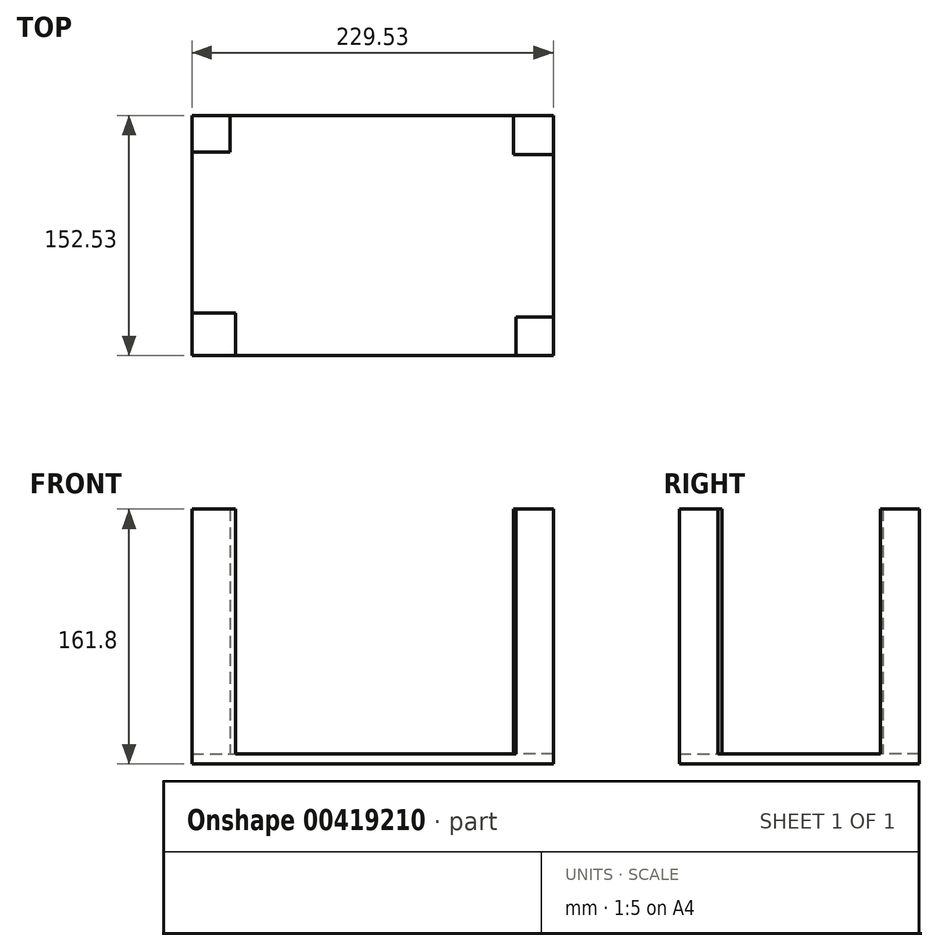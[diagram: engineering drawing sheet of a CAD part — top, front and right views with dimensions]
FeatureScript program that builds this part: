
annotation { "Feature Type Name" : "Feature", "Feature Type Description" : "" }
export const myFeature = defineFeature(function(context is Context, id is Id, definition is map)
    precondition{}
    {
        {
            var Q0;
            Q0=qCreatedBy(makeId("Top.planeOp"),FACE);
            var sketch = newSketch(context, id + "F0", { "sketchPlane" : qUnion([Q0])});
            skLineSegment(sketch, "E0.bottom", {"start": v(-106.06, -80.8) * mm, "end": v(123.47, -80.8) * mm});
            skLineSegment(sketch, "E0.top", {"start": v(-106.06, 71.73) * mm, "end": v(123.47, 71.73) * mm});
            skLineSegment(sketch, "E0.left", {"start": v(-106.06, -80.8) * mm, "end": v(-106.06, 71.73) * mm});
            skLineSegment(sketch, "E0.right", {"start": v(123.47, -80.8) * mm, "end": v(123.47, 71.73) * mm});
            skSolve(sketch);
        }
        {
            var Q0;
            Q0=makeQuery(id+"F0.imprint","IMPRINT",FACE,{"disambiguationData":[TD([[makeQuery(id+"F0.imprint","IMPRINT",EDGE,{"derivedFrom":sQuery(id+"F0.wireOp",EDGE,"E0.bottom")}),1.0]])]});
            extrude(context, id + "F1", {"entities" : qUnion([Q0]), "depth" : 6.35 * mm});
        }
        {
            var Q0;
            Q0=makeQuery(id+"F1.opExtrude","CAP_FACE",FACE,{"disambiguationData":[OSD([sQuery(id+"F0.wireOp",EDGE,"E0.bottom"),sQuery(id+"F0.wireOp",EDGE,"E0.top"),sQuery(id+"F0.wireOp",EDGE,"E0.left"),sQuery(id+"F0.wireOp",EDGE,"E0.right")])],"isStart":false});
            var sketch = newSketch(context, id + "F2", { "sketchPlane" : qUnion([Q0])});
            skLineSegment(sketch, "E1.bottom", {"start": v(123.47, -80.8) * mm, "end": v(99.75, -80.8) * mm});
            skLineSegment(sketch, "E1.top", {"start": v(123.47, -56.12) * mm, "end": v(99.75, -56.12) * mm});
            skLineSegment(sketch, "E1.left", {"start": v(123.47, -80.8) * mm, "end": v(123.47, -56.12) * mm});
            skLineSegment(sketch, "E1.right", {"start": v(99.75, -80.8) * mm, "end": v(99.75, -56.12) * mm});
            skSolve(sketch);
        }
        {
            var Q0;
            Q0=makeQuery(id+"F2.imprint","IMPRINT",FACE,{"disambiguationData":[TD([[makeQuery(id+"F2.imprint","IMPRINT",EDGE,{"derivedFrom":sQuery(id+"F2.wireOp",EDGE,"E1.bottom")}),1.0]])]});
            extrude(context, id + "F3", {"entities" : qUnion([Q0]), "operationType" : NewBodyOperationType.ADD, "depth" : 155.45 * mm});
        }
        {
            var Q0;
            Q0=makeQuery(id+"F1.opExtrude","CAP_FACE",FACE,{"disambiguationData":[OSD([sQuery(id+"F0.wireOp",EDGE,"E0.bottom"),sQuery(id+"F0.wireOp",EDGE,"E0.top"),sQuery(id+"F0.wireOp",EDGE,"E0.left"),sQuery(id+"F0.wireOp",EDGE,"E0.right")])],"isStart":false});
            var sketch = newSketch(context, id + "F4", { "sketchPlane" : qUnion([Q0])});
            skLineSegment(sketch, "E2.bottom", {"start": v(123.47, 71.73) * mm, "end": v(98.13, 71.73) * mm});
            skLineSegment(sketch, "E2.top", {"start": v(123.47, 46.92) * mm, "end": v(98.13, 46.92) * mm});
            skLineSegment(sketch, "E2.left", {"start": v(123.47, 71.73) * mm, "end": v(123.47, 46.92) * mm});
            skLineSegment(sketch, "E2.right", {"start": v(98.13, 71.73) * mm, "end": v(98.13, 46.92) * mm});
            skSolve(sketch);
        }
        {
            var Q0;
            Q0=makeQuery(id+"F4.imprint","IMPRINT",FACE,{"disambiguationData":[TD([[makeQuery(id+"F4.imprint","IMPRINT",EDGE,{"derivedFrom":sQuery(id+"F4.wireOp",EDGE,"E2.bottom")}),-1.0]])]});
            extrude(context, id + "F5", {"entities" : qUnion([Q0]), "operationType" : NewBodyOperationType.ADD, "depth" : 155.45 * mm});
        }
        {
            var Q0;
            Q0=makeQuery(id+"F1.opExtrude","CAP_FACE",FACE,{"disambiguationData":[OSD([sQuery(id+"F0.wireOp",EDGE,"E0.bottom"),sQuery(id+"F0.wireOp",EDGE,"E0.top"),sQuery(id+"F0.wireOp",EDGE,"E0.left"),sQuery(id+"F0.wireOp",EDGE,"E0.right")])],"isStart":false});
            var sketch = newSketch(context, id + "F6", { "sketchPlane" : qUnion([Q0])});
            skLineSegment(sketch, "E3.bottom", {"start": v(-106.06, -80.8) * mm, "end": v(-78.36, -80.8) * mm});
            skLineSegment(sketch, "E3.top", {"start": v(-106.06, -53.76) * mm, "end": v(-78.36, -53.76) * mm});
            skLineSegment(sketch, "E3.left", {"start": v(-106.06, -80.8) * mm, "end": v(-106.06, -53.76) * mm});
            skLineSegment(sketch, "E3.right", {"start": v(-78.36, -80.8) * mm, "end": v(-78.36, -53.76) * mm});
            skLineSegment(sketch, "E4.bottom", {"start": v(-106.06, 71.73) * mm, "end": v(-81.98, 71.73) * mm});
            skLineSegment(sketch, "E4.top", {"start": v(-106.06, 48.5) * mm, "end": v(-81.98, 48.5) * mm});
            skLineSegment(sketch, "E4.left", {"start": v(-106.06, 71.73) * mm, "end": v(-106.06, 48.5) * mm});
            skLineSegment(sketch, "E4.right", {"start": v(-81.98, 71.73) * mm, "end": v(-81.98, 48.5) * mm});
            skSolve(sketch);
        }
        {
            var Q0;
            Q0 = qSketchRegion(id + "F6", true);
            extrude(context, id + "F7", {"entities" : qUnion([Q0]), "operationType" : NewBodyOperationType.ADD, "depth" : 155.45 * mm});
        }
    });
